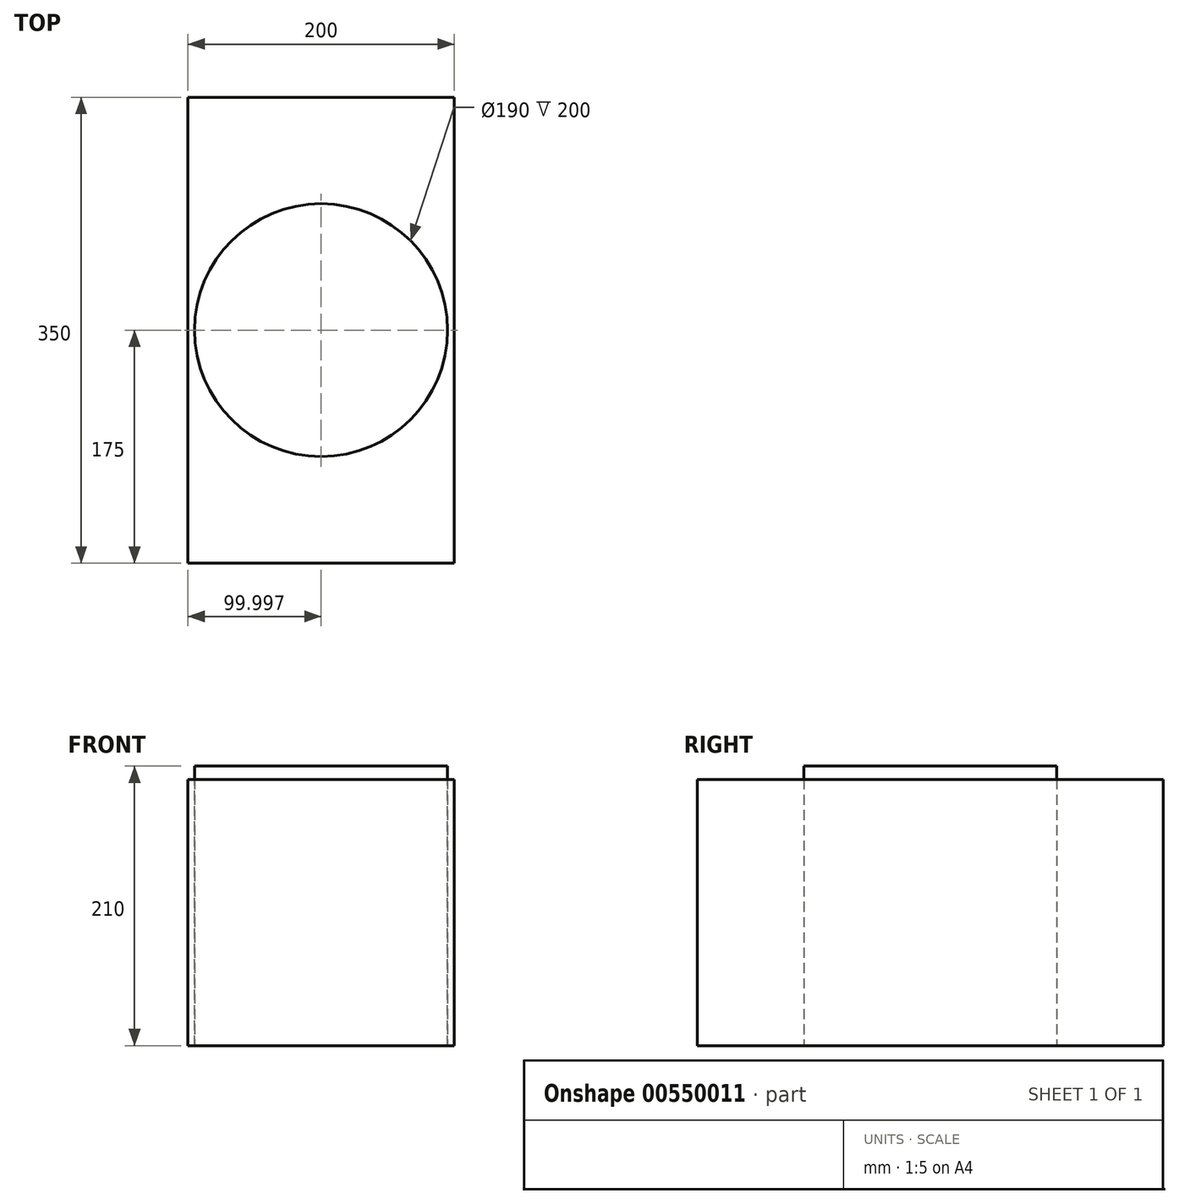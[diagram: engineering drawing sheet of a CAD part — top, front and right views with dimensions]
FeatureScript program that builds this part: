
annotation { "Feature Type Name" : "Feature", "Feature Type Description" : "" }
export const myFeature = defineFeature(function(context is Context, id is Id, definition is map)
    precondition{}
    {
        {
            assignVariable(context, id + "F0", {"name" : "Hojd", "anyValue" : 200});
        }
        {
            assignVariable(context, id + "F1", {"name" : "Laangd", "anyValue" : getVariable(context, 'Hojd') + 500});
        }
        {
            assignVariable(context, id + "F2", {"name" : "Bredd", "anyValue" : getVariable(context, 'Hojd')});
        }
        {
            var Q0;
            Q0=qCreatedBy(makeId("Front.planeOp"),FACE);
            var sketch = newSketch(context, id + "F3", { "sketchPlane" : qUnion([Q0])});
            skLineSegment(sketch, "E0.bottom", {"start": v(52.59, -100) * mm, "end": v(-147.41, -100) * mm});
            skLineSegment(sketch, "E0.top", {"start": v(52.59, 100) * mm, "end": v(-147.41, 100) * mm});
            skLineSegment(sketch, "E0.left", {"start": v(52.59, -100) * mm, "end": v(52.59, 100) * mm});
            skLineSegment(sketch, "E0.right", {"start": v(-147.41, -100) * mm, "end": v(-147.41, 100) * mm});
            skPoint(sketch, "E0.middle", {"position": v(-47.41, 0) * mm});
            skSolve(sketch);
        }
        {
            var Q0;
            Q0 = qSketchRegion(id + "F3", true);
            extrude(context, id + "F4", {"entities" : qUnion([Q0]), "depth" : (getVariable(context, 'Laangd') / 2) * mm, "offsetDistance" : 25 * mm});
        }
        {
            var Q0;
            Q0=makeQuery(id+"F4.opExtrude","SWEPT_FACE",FACE,{"disambiguationData":[OSD([sQuery(id+"F3.wireOp",EDGE,"E0.top")])]});
            var sketch = newSketch(context, id + "F5", { "sketchPlane" : qUnion([Q0])});
            skLineSegment(sketch, "E1.0.0", {"start": v(52.59, 0) * mm, "end": v(-147.41, 0) * mm, "construction": true});
            skLineSegment(sketch, "E1.0.1", {"start": v(-147.41, 0) * mm, "end": v(-147.41, -350) * mm, "construction": true});
            skLineSegment(sketch, "E1.0.2", {"start": v(-147.41, -350) * mm, "end": v(52.59, -350) * mm, "construction": true});
            skLineSegment(sketch, "E1.0.3", {"start": v(52.59, -350) * mm, "end": v(52.59, 0) * mm, "construction": true});
            skLineSegment(sketch, "E2", {"start": v(-47.41, -350) * mm, "end": v(-47.41, 0) * mm, "construction": true});
            skLineSegment(sketch, "E3", {"start": v(-147.41, -175) * mm, "end": v(52.59, -175) * mm, "construction": true});
            skCircle(sketch, "E4", {"center": v(-47.41, -175) * mm, "radius": 95 * mm});
            skSolve(sketch);
        }
        {
            var Q0;
            Q0=makeQuery(id+"F5.imprint","IMPRINT",FACE,{"disambiguationData":[TD([[makeQuery(id+"F5.imprint","IMPRINT",EDGE,{"derivedFrom":sQuery(id+"F5.wireOp",EDGE,"E4")}),1.0]])]});
            extrude(context, id + "F6", {"entities" : qUnion([Q0]), "operationType" : NewBodyOperationType.REMOVE, "endBound" : BoundingType.THROUGH_ALL, "oppositeDirection" : true, "depth" : 25 * mm, "offsetDistance" : 25 * mm});
        }
        {
            var Q0;
            Q0=makeQuery(id+"F4.opExtrude","SWEPT_FACE",FACE,{"disambiguationData":[OSD([sQuery(id+"F3.wireOp",EDGE,"E0.bottom")])]});
            var sketch = newSketch(context, id + "F7", { "sketchPlane" : qUnion([Q0])});
            skLineSegment(sketch, "E5", {"start": v(-147.41, 175) * mm, "end": v(52.59, 175) * mm, "construction": true});
            skLineSegment(sketch, "E6", {"start": v(-47.41, 270) * mm, "end": v(-47.41, 80) * mm, "construction": true});
            skPoint(sketch, "E6.startSnap0", {"position": v(-47.41, 175) * mm});
            skCircle(sketch, "E7", {"center": v(-47.41, 175) * mm, "radius": 95 * mm});
            skSolve(sketch);
        }
        {
            var Q0;
            Q0=makeQuery(id+"F7.imprint","IMPRINT",FACE,{"disambiguationData":[TD([[makeQuery(id+"F7.imprint","IMPRINT",EDGE,{"derivedFrom":sQuery(id+"F7.wireOp",EDGE,"E7")}),1.0]])]});
            extrude(context, id + "F8", {"entities" : qUnion([Q0]), "oppositeDirection" : true, "depth" : (getVariable(context, 'Bredd') + 10) * mm, "offsetDistance" : 25 * mm});
        }
    });
